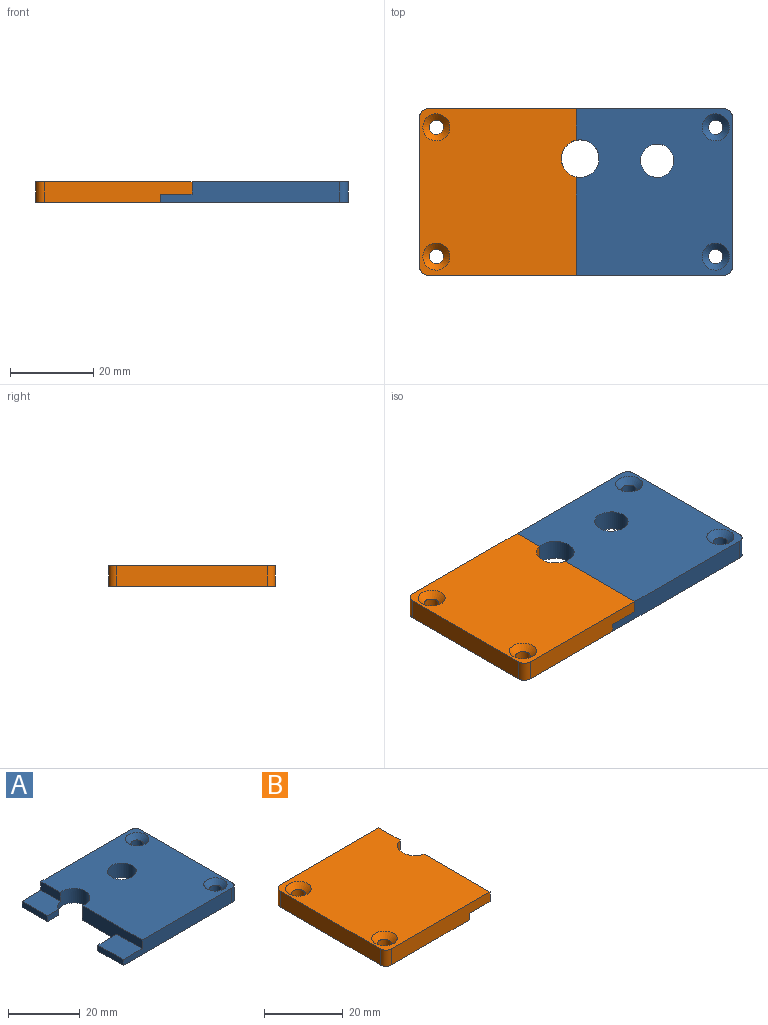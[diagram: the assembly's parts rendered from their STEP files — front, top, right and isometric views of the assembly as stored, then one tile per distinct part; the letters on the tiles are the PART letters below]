
ASSEMBLY  parts=2 mates=1
PART A: 21 faces, bbox 45x40x5 mm
  f0: plane 43x5mm, normal (0,1,0), area 192.5mm2, adj f2,f3,f4,f8,f18,f19
  f1: plane 7.5x2mm, normal (0,1,0), area 15mm2, adj f4,f9,f17,f20
  f2: plane 40x37.5mm, normal (0,0,1), area 1340.9mm2, adj f0,f5,f6,f7,f8,f12,f13,f14
  f3: plane 10x2mm, normal (-1,0,0), area 20mm2, adj f0,f4,f16,f19
  f4: plane 45x40mm, normal (0,0,-1), area 1533.3mm2, adj f0,f1,f3,f5,f6,f7,f8,f9
  f5: plane 43x5mm, normal (0,-1,0), area 192.5mm2, adj f2,f4,f6,f9,f17,f20
  f6: cylinder r=2mm len=5mm, axis (0,0,1), area 15.7mm2, adj f2,f4,f5,f7
  f7: plane 36x5mm, normal (1,0,0), area 180mm2, adj f2,f4,f6,f8
  f8: cylinder r=2mm len=5mm, axis (0,0,1), area 15.7mm2, adj f0,f2,f4,f7
  f9: plane 10x2mm, normal (-1,0,0), area 20mm2, adj f1,f4,f5,f20
  f10: cylinder r=1.75mm len=3.5mm, axis (0,0,1), area 38.5mm2, adj f4,f12
  f11: cylinder r=1.75mm len=3.5mm, axis (0,0,1), area 38.5mm2, adj f4,f13
  f12: cone r=1.75mm half-angle=45deg, axis (0,0,1), area 33.3mm2, adj f2,f10
  f13: cone r=1.75mm half-angle=45deg, axis (0,0,1), area 33.3mm2, adj f2,f11
  f14: cylinder r=4.5mm len=9mm, axis (0,0,1), area 88.7mm2, adj f2,f4,f16,f17,f18,f19
  f15: cylinder r=4mm len=8mm, axis (0,0,1), area 125.7mm2, adj f2,f4
  f16: plane 4.47x2mm, normal (0,-1,0), area 8.9mm2, adj f3,f4,f14,f19
  f17: plane 23.61x5mm, normal (-1,0,0), area 98.1mm2, adj f1,f2,f4,f5,f14,f20
  f18: plane 7.61x3mm, normal (-1,0,0), area 22.8mm2, adj f0,f2,f14,f19
  f19: plane 10x7.5mm, normal (0,0,1), area 70.3mm2, adj f0,f3,f14,f16,f18
  f20: plane 10x7.5mm, normal (0,0,1), area 75mm2, adj f1,f5,f9,f17
PART B: 20 faces, bbox 37.5x40x5 mm
  f0: plane 35.5x5mm, normal (0,-1,0), area 162.5mm2, adj f2,f5,f8,f13,f18,f19
  f1: plane 35.5x5mm, normal (0,1,0), area 162.5mm2, adj f2,f3,f6,f8,f15,f16
  f2: plane 40x37.5mm, normal (0,0,-1), area 1305mm2, adj f0,f1,f4,f5,f6,f7,f9,f10
  f3: plane 7.61x3mm, normal (1,0,0), area 22.8mm2, adj f1,f4,f8,f16
  f4: cylinder r=4.5mm len=8.78mm, axis (0,0,1), area 51.5mm2, adj f2,f3,f8,f13,f14,f16
  f5: cylinder r=2mm len=5mm, axis (0,0,1), area 15.7mm2, adj f0,f2,f7,f8
  f6: cylinder r=2mm len=5mm, axis (0,0,1), area 15.7mm2, adj f1,f2,f7,f8
  f7: plane 36x5mm, normal (-1,0,0), area 180mm2, adj f2,f5,f6,f8
  f8: plane 40x37.5mm, normal (0,0,1), area 1409mm2, adj f0,f1,f3,f4,f5,f6,f7,f11
  f9: cylinder r=1.75mm len=3.5mm, axis (0,0,1), area 38.5mm2, adj f2,f11
  f10: cylinder r=1.75mm len=3.5mm, axis (0,0,1), area 38.5mm2, adj f2,f12
  f11: cone r=1.75mm half-angle=45deg, axis (0,0,1), area 33.3mm2, adj f8,f9
  f12: cone r=1.75mm half-angle=45deg, axis (0,0,1), area 33.3mm2, adj f8,f10
  f13: plane 23.61x5mm, normal (1,0,0), area 97.1mm2, adj f0,f2,f4,f8,f17,f19
  f14: plane 4.26x2mm, normal (0,1,0), area 8.5mm2, adj f2,f4,f15,f16
  f15: plane 10.5x2mm, normal (1,0,0), area 21mm2, adj f1,f2,f14,f16
  f16: plane 10.5x7.5mm, normal (0,0,-1), area 72.4mm2, adj f1,f3,f4,f14,f15
  f17: plane 7.5x2mm, normal (0,-1,0), area 15mm2, adj f2,f13,f18,f19
  f18: plane 10.5x2mm, normal (1,0,0), area 21mm2, adj f0,f2,f17,f19
  f19: plane 10.5x7.5mm, normal (0,0,-1), area 78.8mm2, adj f0,f13,f17,f18
PLACE A t=(0,-2.1,0)mm
PLACE B t=(0,-2.1,0)mm
MATE fastened B.f8 <-> A.f2  axis (0,0,1) through (0,1.52,5)mm
